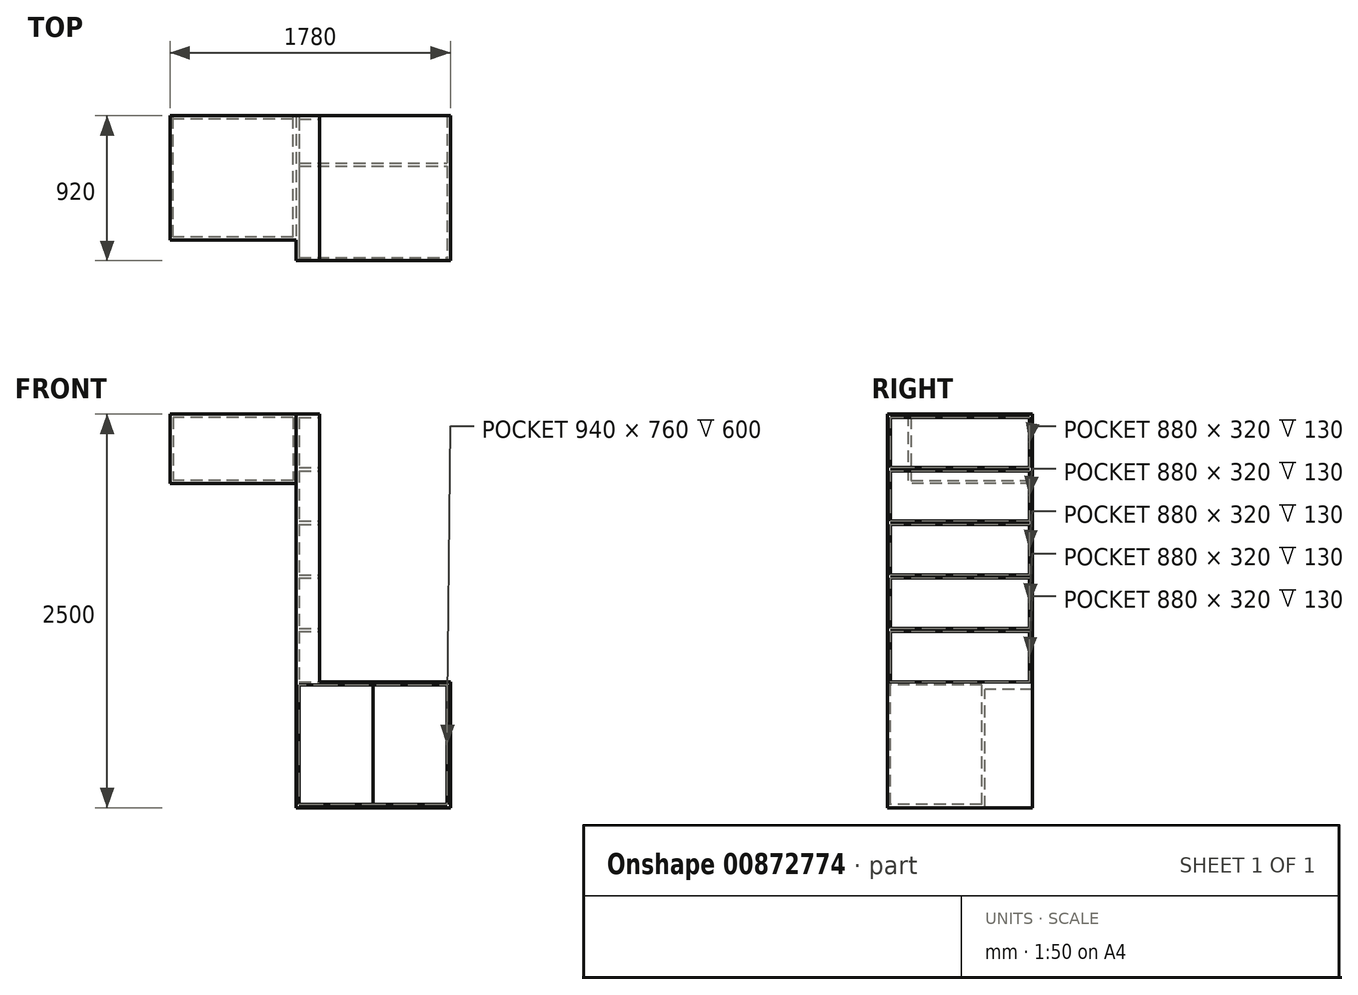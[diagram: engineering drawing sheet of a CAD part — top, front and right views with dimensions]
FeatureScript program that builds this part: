
annotation { "Feature Type Name" : "Feature", "Feature Type Description" : "" }
export const myFeature = defineFeature(function(context is Context, id is Id, definition is map)
    precondition{}
    {
        {
            var Q0;
            Q0=qCreatedBy(makeId("Front.planeOp"),FACE);
            var sketch = newSketch(context, id + "F0", { "sketchPlane" : qUnion([Q0])});
            skLineSegment(sketch, "E0.bottom", {"start": v(-490, 0) * mm, "end": v(490, 0) * mm});
            skLineSegment(sketch, "E0.top", {"start": v(-490, 800) * mm, "end": v(490, 800) * mm});
            skLineSegment(sketch, "E0.left", {"start": v(-490, 0) * mm, "end": v(-490, 800) * mm});
            skLineSegment(sketch, "E0.right", {"start": v(490, 0) * mm, "end": v(490, 800) * mm});
            skLineSegment(sketch, "E1.bottom", {"start": v(-470, 780) * mm, "end": v(470, 780) * mm});
            skLineSegment(sketch, "E1.top", {"start": v(-470, 20) * mm, "end": v(470, 20) * mm});
            skLineSegment(sketch, "E1.left", {"start": v(-470, 780) * mm, "end": v(-470, 20) * mm});
            skLineSegment(sketch, "E1.right", {"start": v(470, 780) * mm, "end": v(470, 20) * mm});
            skLineSegment(sketch, "E2", {"start": v(-470, 400) * mm, "end": v(470, 400) * mm, "construction": true});
            skLineSegment(sketch, "E3", {"start": v(0, 20) * mm, "end": v(0, 780) * mm});
            skSolve(sketch);
        }
        {
            var Q0;
            {var subQ0=sQuery(id+"F0.wireOp",EDGE,"E1.left");Q0=makeQuery(id+"F0.imprint","IMPRINT",FACE,{"disambiguationData":[TD([[makeQuery(id+"F0.imprint","IMPRINT",EDGE,{"derivedFrom":subQ0}),1.0]])]});}
            var Q1;
            {var subQ0=sQuery(id+"F0.wireOp",EDGE,"E1.right");Q1=makeQuery(id+"F0.imprint","IMPRINT",FACE,{"disambiguationData":[TD([[makeQuery(id+"F0.imprint","IMPRINT",EDGE,{"derivedFrom":subQ0}),-1.0]])]});}
            var Q2;
            Q2=makeQuery(id+"F0.imprint","IMPRINT",FACE,{"disambiguationData":[TD([[makeQuery(id+"F0.imprint","IMPRINT",EDGE,{"derivedFrom":sQuery(id+"F0.wireOp",EDGE,"E0.bottom")}),1.0]])]});
            extrude(context, id + "F1", {"entities" : qUnion([Q0, Q1, Q2]), "oppositeDirection" : true, "depth" : 620 * mm, "offsetDistance" : 25 * mm});
        }
        {
            var Q0;
            Q0=makeQuery(id+"F1.opExtrude","CAP_FACE",FACE,{"disambiguationData":[OSD([sQuery(id+"F0.wireOp",EDGE,"E0.bottom"),sQuery(id+"F0.wireOp",EDGE,"E0.top"),sQuery(id+"F0.wireOp",EDGE,"E0.left"),sQuery(id+"F0.wireOp",EDGE,"E0.right")])],"isStart":true});
            shell(context, id + "F2", {"entities" : qUnion([Q0]), "thickness" : 20 * mm});
        }
        {
            var Q0;
            {var subQ0=sQuery(id+"F0.wireOp",EDGE,"E1.left");Q0=makeQuery(id+"F0.imprint","IMPRINT",FACE,{"disambiguationData":[TD([[makeQuery(id+"F0.imprint","IMPRINT",EDGE,{"derivedFrom":subQ0}),1.0]])]});}
            extrude(context, id + "F3", {"entities" : qUnion([Q0]), "oppositeDirection" : true, "depth" : 20 * mm, "offsetDistance" : 25 * mm});
        }
        {
            var Q0;
            {var subQ0=sQuery(id+"F0.wireOp",EDGE,"E1.right");Q0=makeQuery(id+"F0.imprint","IMPRINT",FACE,{"disambiguationData":[TD([[makeQuery(id+"F0.imprint","IMPRINT",EDGE,{"derivedFrom":subQ0}),-1.0]])]});}
            extrude(context, id + "F4", {"entities" : qUnion([Q0]), "oppositeDirection" : true, "depth" : 20 * mm, "offsetDistance" : 25 * mm});
        }
        {
            var Q0;
            Q0=makeQuery(id+"F1.opExtrude","CAP_FACE",FACE,{"disambiguationData":[OSD([sQuery(id+"F0.wireOp",EDGE,"E0.bottom"),sQuery(id+"F0.wireOp",EDGE,"E0.top"),sQuery(id+"F0.wireOp",EDGE,"E0.left"),sQuery(id+"F0.wireOp",EDGE,"E0.right")])],"isStart":false});
            var sketch = newSketch(context, id + "F5", { "sketchPlane" : qUnion([Q0])});
            skLineSegment(sketch, "E4.bottom", {"start": v(-470, 0) * mm, "end": v(470, 0) * mm});
            skLineSegment(sketch, "E4.top", {"start": v(-470, 750) * mm, "end": v(470, 750) * mm});
            skLineSegment(sketch, "E4.left", {"start": v(-470, 0) * mm, "end": v(-470, 750) * mm});
            skLineSegment(sketch, "E4.right", {"start": v(470, 0) * mm, "end": v(470, 750) * mm});
            skSolve(sketch);
        }
        {
            var Q0;
            Q0=makeQuery(id+"F5.imprint","IMPRINT",FACE,{"disambiguationData":[TD([[makeQuery(id+"F5.imprint","IMPRINT",EDGE,{"derivedFrom":sQuery(id+"F5.wireOp",EDGE,"E4.top")}),1.0]])]});
            extrude(context, id + "F6", {"entities" : qUnion([Q0]), "operationType" : NewBodyOperationType.ADD, "depth" : 300 * mm, "offsetDistance" : 25 * mm});
        }
        {
            var Q0;
            {var subQ0=sQuery(id+"F0.wireOp",EDGE,"E0.top");Q0=makeQuery(id+"F6.boolean.opBoolean","MERGE",FACE,{"derivedFrom":[makeQuery(id+"F1.opExtrude","SWEPT_FACE",FACE,{"disambiguationData":[OSD([subQ0])]}),makeQuery(id+"F6.opExtrude","SWEPT_FACE",FACE,{"disambiguationData":[OSD([subQ0])]})]});}
            var sketch = newSketch(context, id + "F7", { "sketchPlane" : qUnion([Q0])});
            skLineSegment(sketch, "E5.bottom", {"start": v(-490, 0) * mm, "end": v(-340, 0) * mm});
            skLineSegment(sketch, "E5.top", {"start": v(-490, 920) * mm, "end": v(-340, 920) * mm});
            skLineSegment(sketch, "E5.left", {"start": v(-490, 0) * mm, "end": v(-490, 920) * mm});
            skLineSegment(sketch, "E5.right", {"start": v(-340, 0) * mm, "end": v(-340, 920) * mm});
            skSolve(sketch);
        }
        {
            var Q0;
            Q0=makeQuery(id+"F7.imprint","IMPRINT",FACE,{"disambiguationData":[TD([[makeQuery(id+"F7.imprint","IMPRINT",EDGE,{"derivedFrom":sQuery(id+"F7.wireOp",EDGE,"E5.bottom")}),1.0]])]});
            extrude(context, id + "F8", {"entities" : qUnion([Q0]), "operationType" : NewBodyOperationType.ADD, "depth" : 1700 * mm, "offsetDistance" : 25 * mm});
        }
        {
            var Q0;
            Q0=makeQuery(id+"F8.opExtrude","SWEPT_FACE",FACE,{"disambiguationData":[OSD([sQuery(id+"F7.wireOp",EDGE,"E5.right")])]});
            var sketch = newSketch(context, id + "F9", { "sketchPlane" : qUnion([Q0])});
            skLineSegment(sketch, "E6.bottom", {"start": v(20, 800) * mm, "end": v(900, 800) * mm});
            skLineSegment(sketch, "E6.top", {"start": v(20, 1120) * mm, "end": v(900, 1120) * mm});
            skLineSegment(sketch, "E6.left", {"start": v(20, 800) * mm, "end": v(20, 1120) * mm});
            skLineSegment(sketch, "E6.right", {"start": v(900, 800) * mm, "end": v(900, 1120) * mm});
            skLineSegment(sketch, "E7", {"start": v(460, 800) * mm, "end": v(460, 2500) * mm, "construction": true});
            skLineSegment(sketch, "E8.bottom", {"start": v(20, 1140) * mm, "end": v(900, 1140) * mm});
            skLineSegment(sketch, "E8.top", {"start": v(20, 1460) * mm, "end": v(900, 1460) * mm});
            skLineSegment(sketch, "E8.left", {"start": v(20, 1140) * mm, "end": v(20, 1460) * mm});
            skLineSegment(sketch, "E8.right", {"start": v(900, 1140) * mm, "end": v(900, 1460) * mm});
            skLineSegment(sketch, "E9.bottom", {"start": v(20, 1480) * mm, "end": v(900, 1480) * mm});
            skLineSegment(sketch, "E9.top", {"start": v(20, 1800) * mm, "end": v(900, 1800) * mm});
            skLineSegment(sketch, "E9.left", {"start": v(20, 1480) * mm, "end": v(20, 1800) * mm});
            skLineSegment(sketch, "E9.right", {"start": v(900, 1480) * mm, "end": v(900, 1800) * mm});
            skLineSegment(sketch, "E10.bottom", {"start": v(20, 1820) * mm, "end": v(900, 1820) * mm});
            skLineSegment(sketch, "E10.top", {"start": v(20, 2140) * mm, "end": v(900, 2140) * mm});
            skLineSegment(sketch, "E10.left", {"start": v(20, 1820) * mm, "end": v(20, 2140) * mm});
            skLineSegment(sketch, "E10.right", {"start": v(900, 1820) * mm, "end": v(900, 2140) * mm});
            skLineSegment(sketch, "E11.bottom", {"start": v(20, 2160) * mm, "end": v(900, 2160) * mm});
            skLineSegment(sketch, "E11.top", {"start": v(20, 2480) * mm, "end": v(900, 2480) * mm});
            skLineSegment(sketch, "E11.left", {"start": v(20, 2160) * mm, "end": v(20, 2480) * mm});
            skLineSegment(sketch, "E11.right", {"start": v(900, 2160) * mm, "end": v(900, 2480) * mm});
            skLineSegment(sketch, "E12", {"start": v(20, 960) * mm, "end": v(900, 960) * mm, "construction": true});
            skLineSegment(sketch, "E13", {"start": v(20, 1300) * mm, "end": v(900, 1300) * mm, "construction": true});
            skLineSegment(sketch, "E14", {"start": v(20, 1640) * mm, "end": v(900, 1640) * mm, "construction": true});
            skLineSegment(sketch, "E15", {"start": v(20, 1980) * mm, "end": v(900, 1980) * mm, "construction": true});
            skLineSegment(sketch, "E16", {"start": v(20, 2320) * mm, "end": v(900, 2320) * mm, "construction": true});
            skLineSegment(sketch, "E17", {"start": v(-22.34, 1130) * mm, "end": v(962.8, 1130) * mm, "construction": true});
            skLineSegment(sketch, "E18", {"start": v(-28.68, 1470) * mm, "end": v(953.06, 1470) * mm, "construction": true});
            skLineSegment(sketch, "E19", {"start": v(-38.17, 1810) * mm, "end": v(988.24, 1810) * mm, "construction": true});
            skSolve(sketch);
        }
        {
            var Q0;
            Q0=makeQuery(id+"F9.imprint","IMPRINT",FACE,{"disambiguationData":[TD([[makeQuery(id+"F9.imprint","IMPRINT",EDGE,{"derivedFrom":sQuery(id+"F9.wireOp",EDGE,"E6.bottom")}),1.0]])]});
            var Q1;
            Q1=makeQuery(id+"F9.imprint","IMPRINT",FACE,{"disambiguationData":[TD([[makeQuery(id+"F9.imprint","IMPRINT",EDGE,{"derivedFrom":sQuery(id+"F9.wireOp",EDGE,"E8.bottom")}),1.0]])]});
            var Q2;
            Q2=makeQuery(id+"F9.imprint","IMPRINT",FACE,{"disambiguationData":[TD([[makeQuery(id+"F9.imprint","IMPRINT",EDGE,{"derivedFrom":sQuery(id+"F9.wireOp",EDGE,"E9.bottom")}),1.0]])]});
            var Q3;
            Q3=makeQuery(id+"F9.imprint","IMPRINT",FACE,{"disambiguationData":[TD([[makeQuery(id+"F9.imprint","IMPRINT",EDGE,{"derivedFrom":sQuery(id+"F9.wireOp",EDGE,"E10.bottom")}),1.0]])]});
            var Q4;
            Q4=makeQuery(id+"F9.imprint","IMPRINT",FACE,{"disambiguationData":[TD([[makeQuery(id+"F9.imprint","IMPRINT",EDGE,{"derivedFrom":sQuery(id+"F9.wireOp",EDGE,"E11.bottom")}),1.0]])]});
            extrude(context, id + "F10", {"entities" : qUnion([Q0, Q1, Q2, Q3, Q4]), "operationType" : NewBodyOperationType.REMOVE, "endBound" : BoundingType.UP_TO_NEXT, "oppositeDirection" : true, "depth" : 25 * mm, "hasOffset" : true, "offsetDistance" : 20 * mm});
        }
        {
            var Q0;
            {var subQ0=sQuery(id+"F0.wireOp",EDGE,"E0.left");Q0=makeQuery(id+"F8.boolean.opBoolean","MERGE",FACE,{"derivedFrom":[makeQuery(id+"F6.boolean.opBoolean","MERGE",FACE,{"derivedFrom":[makeQuery(id+"F1.opExtrude","SWEPT_FACE",FACE,{"disambiguationData":[OSD([subQ0])]}),makeQuery(id+"F6.opExtrude","SWEPT_FACE",FACE,{"disambiguationData":[OSD([subQ0])]})]}),makeQuery(id+"F8.opExtrude","SWEPT_FACE",FACE,{"disambiguationData":[OSD([sQuery(id+"F7.wireOp",EDGE,"E5.left")])]})]});}
            var sketch = newSketch(context, id + "F11", { "sketchPlane" : qUnion([Q0])});
            skLineSegment(sketch, "E20.bottom", {"start": v(-920, 2500) * mm, "end": v(-130, 2500) * mm});
            skLineSegment(sketch, "E20.top", {"start": v(-920, 2060) * mm, "end": v(-130, 2060) * mm});
            skLineSegment(sketch, "E20.left", {"start": v(-920, 2500) * mm, "end": v(-920, 2060) * mm});
            skLineSegment(sketch, "E20.right", {"start": v(-130, 2500) * mm, "end": v(-130, 2060) * mm});
            skSolve(sketch);
        }
        {
            var Q0;
            Q0=makeQuery(id+"F11.imprint","IMPRINT",FACE,{"disambiguationData":[TD([[makeQuery(id+"F11.imprint","IMPRINT",EDGE,{"derivedFrom":sQuery(id+"F11.wireOp",EDGE,"E20.bottom")}),-1.0]])]});
            extrude(context, id + "F12", {"entities" : qUnion([Q0]), "operationType" : NewBodyOperationType.ADD, "depth" : 800 * mm, "offsetDistance" : 25 * mm});
        }
        {
            var Q0;
            Q0=makeQuery(id+"F12.boolean.opBoolean","MERGE",FACE,{"derivedFrom":[makeQuery(id+"F8.boolean.opBoolean","MERGE",FACE,{"derivedFrom":[makeQuery(id+"F6.opExtrude","CAP_FACE",FACE,{"disambiguationData":[OSD([sQuery(id+"F0.wireOp",EDGE,"E0.bottom"),sQuery(id+"F0.wireOp",EDGE,"E0.top"),sQuery(id+"F0.wireOp",EDGE,"E0.left"),sQuery(id+"F0.wireOp",EDGE,"E0.right"),sQuery(id+"F5.wireOp",EDGE,"E4.top"),sQuery(id+"F5.wireOp",EDGE,"E4.left"),sQuery(id+"F5.wireOp",EDGE,"E4.right")])],"isStart":false}),makeQuery(id+"F8.opExtrude","SWEPT_FACE",FACE,{"disambiguationData":[OSD([sQuery(id+"F7.wireOp",EDGE,"E5.top")])]})]}),makeQuery(id+"F12.opExtrude","SWEPT_FACE",FACE,{"disambiguationData":[OSD([sQuery(id+"F11.wireOp",EDGE,"E20.left")])]})]});
            var sketch = newSketch(context, id + "F13", { "sketchPlane" : qUnion([Q0])});
            skLineSegment(sketch, "E21.bottom", {"start": v(510, 2480) * mm, "end": v(1270, 2480) * mm});
            skLineSegment(sketch, "E21.top", {"start": v(510, 2080) * mm, "end": v(1270, 2080) * mm});
            skLineSegment(sketch, "E21.left", {"start": v(510, 2480) * mm, "end": v(510, 2080) * mm});
            skLineSegment(sketch, "E21.right", {"start": v(1270, 2480) * mm, "end": v(1270, 2080) * mm});
            skSolve(sketch);
        }
        {
            var Q0;
            Q0=makeQuery(id+"F13.imprint","IMPRINT",FACE,{"disambiguationData":[TD([[makeQuery(id+"F13.imprint","IMPRINT",EDGE,{"derivedFrom":sQuery(id+"F13.wireOp",EDGE,"E21.bottom")}),-1.0]])]});
            extrude(context, id + "F14", {"entities" : qUnion([Q0]), "operationType" : NewBodyOperationType.REMOVE, "endBound" : BoundingType.UP_TO_NEXT, "oppositeDirection" : true, "depth" : 25 * mm, "hasOffset" : true, "offsetDistance" : 20 * mm});
        }
        {
            var Q0;
            Q0 = qSketchRegion(id + "F13", true);
            extrude(context, id + "F15", {"entities" : qUnion([Q0]), "oppositeDirection" : true, "depth" : 20 * mm, "offsetDistance" : 25 * mm});
        }
    });
